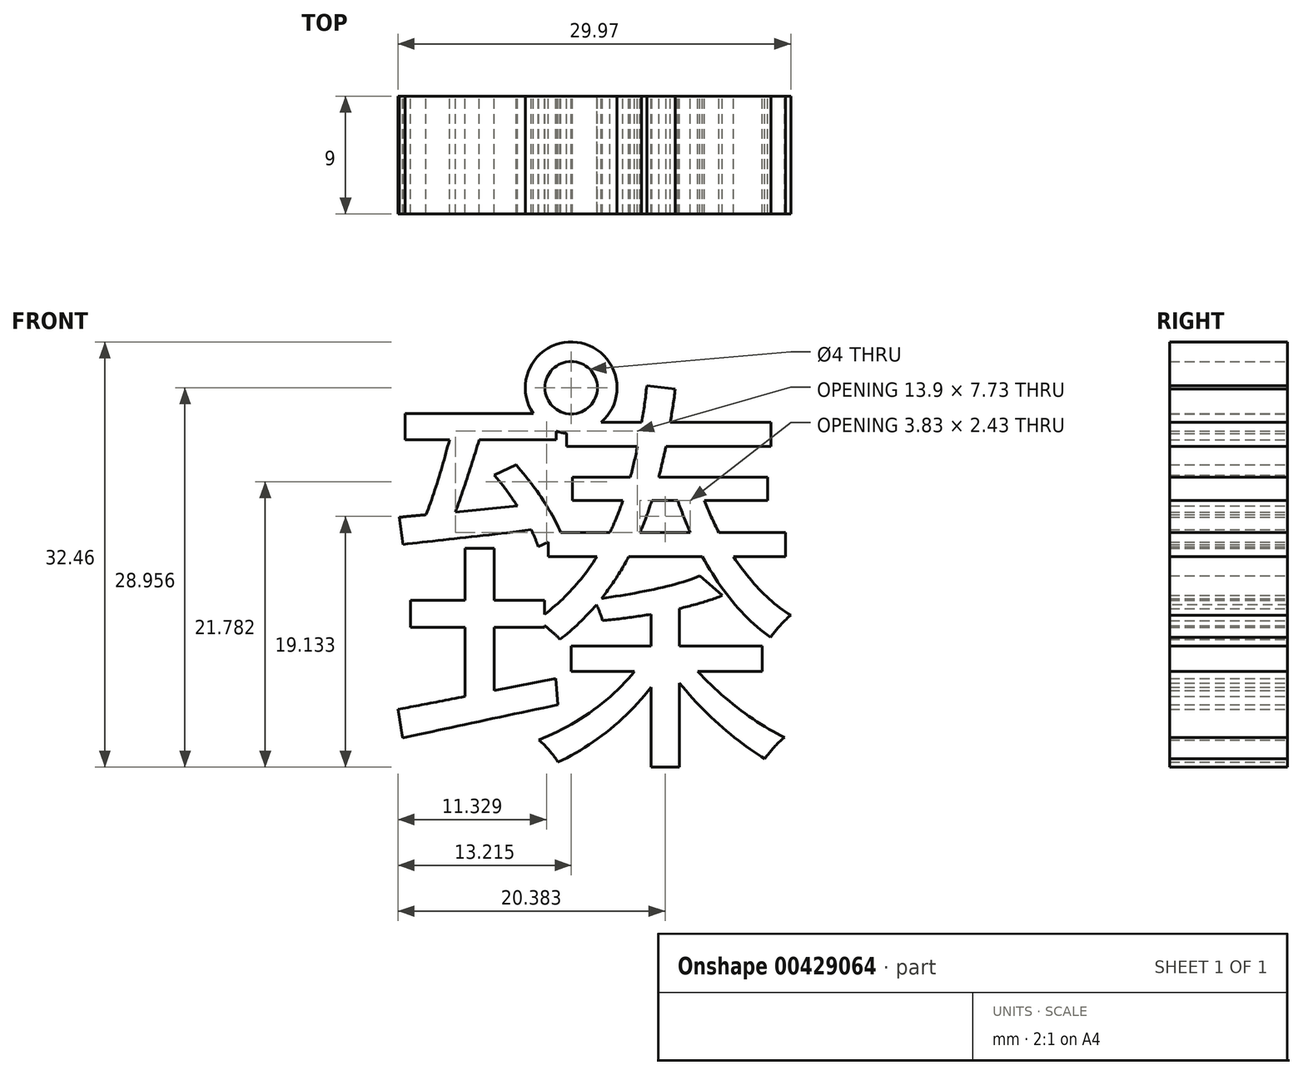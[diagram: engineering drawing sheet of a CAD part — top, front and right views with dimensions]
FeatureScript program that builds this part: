
annotation { "Feature Type Name" : "Feature", "Feature Type Description" : "" }
export const myFeature = defineFeature(function(context is Context, id is Id, definition is map)
    precondition{}
    {
        {
            var Q0;
            Q0=qCreatedBy(makeId("Front.planeOp"),FACE);
            var sketch = newSketch(context, id + "F0", { "sketchPlane" : qUnion([Q0])});
            skText(sketch, "E0", { "text": "臻", "fontName": "NotoSansCJKjp-Regular.otf"});
            skCircle(sketch, "E1", {"center": v(-1.92, 14.96) * mm, "radius": 3.5 * mm});
            skCircle(sketch, "E2", {"center": v(-1.92, 14.96) * mm, "radius": 2 * mm});
            const initialGuessF0  = {"E0": [-0.01618, -0.01167, 1, 0, 0.023]};
            skSetInitialGuess(sketch, initialGuessF0);
            skSolve(sketch);
        }
        {
            var Q0;
            Q0 = qSketchRegion(id + "F0", true);
            extrude(context, id + "F1", {"entities" : qUnion([Q0]), "depth" : 9 * mm});
        }
    });
